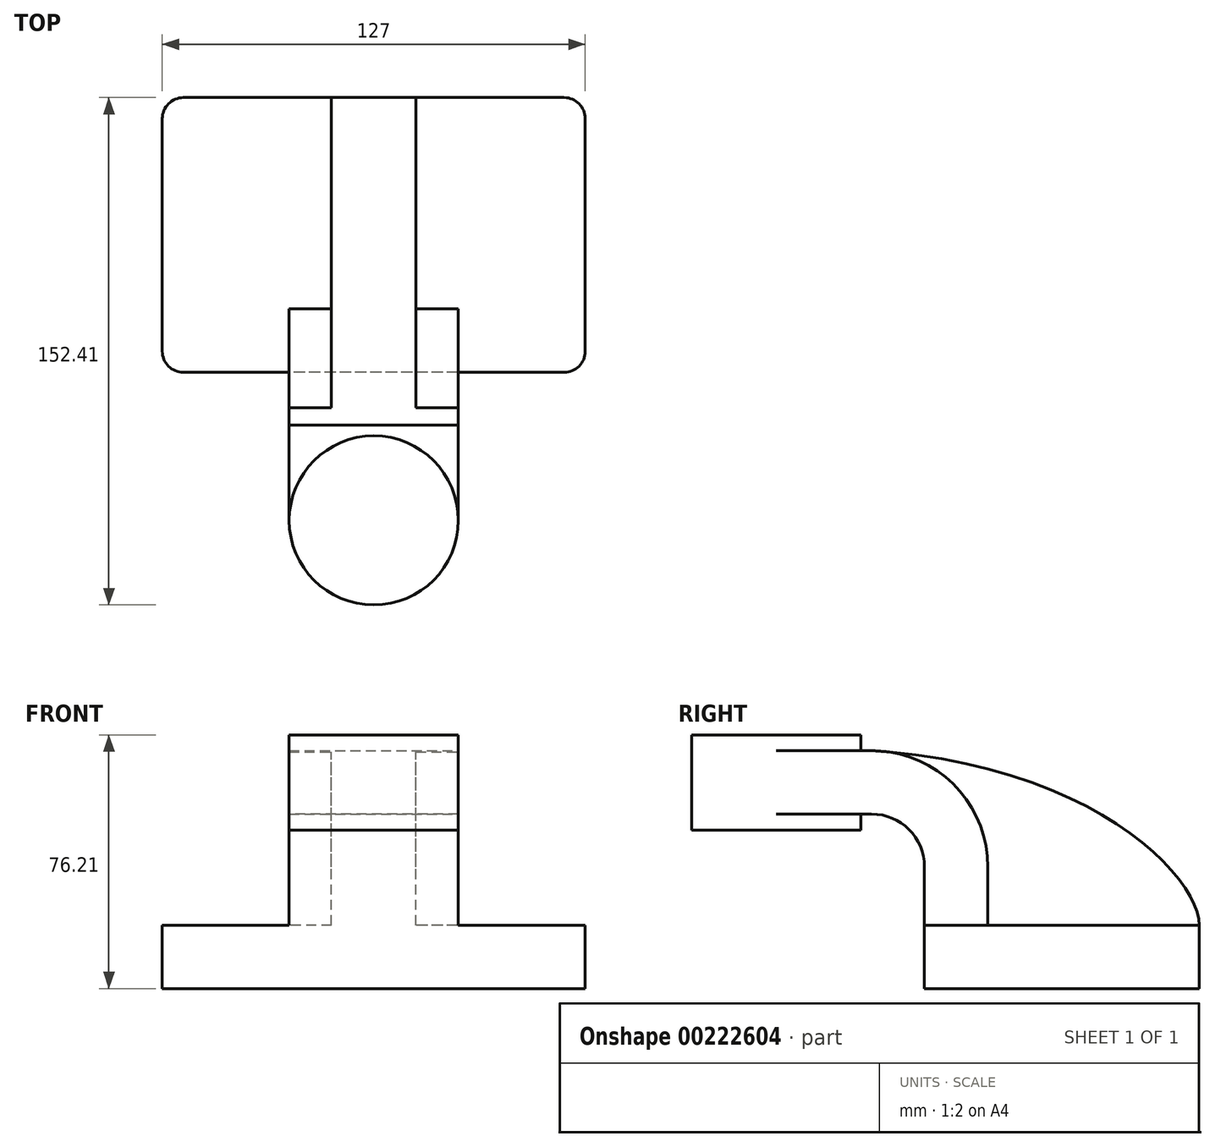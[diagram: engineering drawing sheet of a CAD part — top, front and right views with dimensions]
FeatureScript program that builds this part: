
annotation { "Feature Type Name" : "Feature", "Feature Type Description" : "" }
export const myFeature = defineFeature(function(context is Context, id is Id, definition is map)
    precondition{}
    {
        {
            var Q0;
            Q0=qCreatedBy(makeId("Right.planeOp"),FACE);
            var sketch = newSketch(context, id + "F0", { "sketchPlane" : qUnion([Q0])});
            skLineSegment(sketch, "E0.bottom", {"start": v(-41.28, -9.52) * mm, "end": v(41.28, -9.52) * mm});
            skLineSegment(sketch, "E0.top", {"start": v(-41.28, 9.53) * mm, "end": v(41.28, 9.53) * mm});
            skLineSegment(sketch, "E0.left", {"start": v(-41.27, -9.52) * mm, "end": v(-41.28, 9.53) * mm});
            skLineSegment(sketch, "E0.right", {"start": v(41.28, -9.52) * mm, "end": v(41.28, 9.53) * mm});
            skPoint(sketch, "E0.middle", {"position": v(0, 0) * mm});
            skLineSegment(sketch, "E1.bottom", {"start": v(-111.13, 38.1) * mm, "end": v(-60.33, 38.1) * mm});
            skLineSegment(sketch, "E1.top", {"start": v(-111.13, 66.68) * mm, "end": v(-60.33, 66.68) * mm});
            skLineSegment(sketch, "E1.left", {"start": v(-111.13, 38.1) * mm, "end": v(-111.13, 66.68) * mm});
            skLineSegment(sketch, "E1.right", {"start": v(-60.33, 38.1) * mm, "end": v(-60.33, 66.68) * mm});
            skPoint(sketch, "E1.middle", {"position": v(-85.73, 52.39) * mm});
            skLineSegment(sketch, "E2", {"start": v(-41.28, 9.53) * mm, "end": v(-41.28, 27) * mm});
            skArc(sketch, "E3", {"start": v(-41.28, 27) * mm, "mid": v(-45.92, 38.23) * mm, "end": v(-57.15, 42.88) * mm});
            skLineSegment(sketch, "E4", {"start": v(-57.15, 42.88) * mm, "end": v(-85.73, 42.88) * mm});
            skLineSegment(sketch, "E5.0", {"start": v(-57.15, 61.93) * mm, "end": v(-85.73, 61.93) * mm});
            skArc(sketch, "E5.1", {"start": v(-22.23, 27) * mm, "mid": v(-32.45, 51.7) * mm, "end": v(-57.15, 61.93) * mm});
            skLineSegment(sketch, "E5.2", {"start": v(-22.23, 9.53) * mm, "end": v(-22.23, 27) * mm});
            skLineSegment(sketch, "E6", {"start": v(-85.73, 66.68) * mm, "end": v(-85.73, 38.1) * mm});
            skFitSpline(sketch, "E7", {"points": [v(41.28, 9.52) * mm, v(-57.15, 61.93) * mm], "startDerivative": vector(0, 41.98) * mm, "endDerivative": vector(-200.82, 12.64) * mm});
            skSolve(sketch);
        }
        {
            var Q0;
            Q0=makeQuery(id+"F0.imprint","IMPRINT",FACE,{"disambiguationData":[TD([[makeQuery(id+"F0.imprint","IMPRINT",EDGE,{"derivedFrom":sQuery(id+"F0.wireOp",EDGE,"E0.bottom")}),1.0]])]});
            extrude(context, id + "F1", {"entities" : qUnion([Q0]), "endBound" : BoundingType.SYMMETRIC, "depth" : 127 * mm});
        }
        {
            var Q0;
            {var subQ1=sQuery(id+"F0.wireOp",EDGE,"E2");Q0=makeQuery(id+"F0.imprint","IMPRINT",FACE,{"disambiguationData":[TD([[makeQuery(id+"F0.imprint","IMPRINT",EDGE,{"derivedFrom":subQ1}),-1.0]])]});}
            var Q1;
            {var subQ0=sQuery(id+"F0.wireOp",EDGE,"E4");var subQ1=sQuery(id+"F0.wireOp",EDGE,"E1.right");var subQ2=makeQuery(id+"F0.imprint","INTERSECT",VERTEX,{"derivedFrom":[subQ1,subQ0]});Q1=makeQuery(id+"F0.imprint","IMPRINT",FACE,{"disambiguationData":[TD([[makeQuery(id+"F0.imprint","IMPRINT",EDGE,{"disambiguationData":[TD([[subQ2,-1.0]])],"derivedFrom":subQ1}),1.0]])]});}
            extrude(context, id + "F2", {"entities" : qUnion([Q0, Q1]), "operationType" : NewBodyOperationType.ADD, "endBound" : BoundingType.SYMMETRIC, "depth" : 50.8 * mm});
        }
        {
            var Q0;
            {var subQ0=sQuery(id+"F0.wireOp",EDGE,"E1.left");Q0=makeQuery(id+"F0.imprint","IMPRINT",FACE,{"disambiguationData":[TD([[makeQuery(id+"F0.imprint","IMPRINT",EDGE,{"derivedFrom":subQ0}),-1.0]])]});}
            var Q1;
            Q1=sQuery(id+"F0.wireOp",EDGE,"E6");
            revolve(context, id + "F3", {"operationType" : NewBodyOperationType.ADD, "entities" : qUnion([Q0]), "axis" : qUnion([Q1]), "revolveType" : RevolveType.FULL});
        }
        {
            var Q0;
            Q0=makeQuery(id+"F0.imprint","IMPRINT",FACE,{"disambiguationData":[TD([[makeQuery(id+"F0.imprint","IMPRINT",EDGE,{"derivedFrom":sQuery(id+"F0.wireOp",EDGE,"E5.1")}),-1.0]])]});
            extrude(context, id + "F4", {"entities" : qUnion([Q0]), "operationType" : NewBodyOperationType.ADD, "endBound" : BoundingType.SYMMETRIC, "depth" : 25.4 * mm});
        }
        {
            var Q0;
            Q0=makeQuery(id+"F1.opExtrude","CAP_EDGE",EDGE,{"disambiguationData":[OSD([sQuery(id+"F0.wireOp",EDGE,"E0.right")])],"isStart":true});
            var Q1;
            Q1=makeQuery(id+"F1.opExtrude","CAP_EDGE",EDGE,{"disambiguationData":[OSD([sQuery(id+"F0.wireOp",EDGE,"E0.left")])],"isStart":true});
            var Q2;
            Q2=makeQuery(id+"F1.opExtrude","CAP_EDGE",EDGE,{"disambiguationData":[OSD([sQuery(id+"F0.wireOp",EDGE,"E0.right")])],"isStart":false});
            var Q3;
            Q3=makeQuery(id+"F1.opExtrude","CAP_EDGE",EDGE,{"disambiguationData":[OSD([sQuery(id+"F0.wireOp",EDGE,"E0.left")])],"isStart":false});
            fillet(context, id + "F5", {"entities" : qUnion([Q0, Q1, Q2, Q3]), "radius" : 6.35 * mm, "tangentPropagation" : true, "allowEdgeOverflow" : false});
        }
    });
